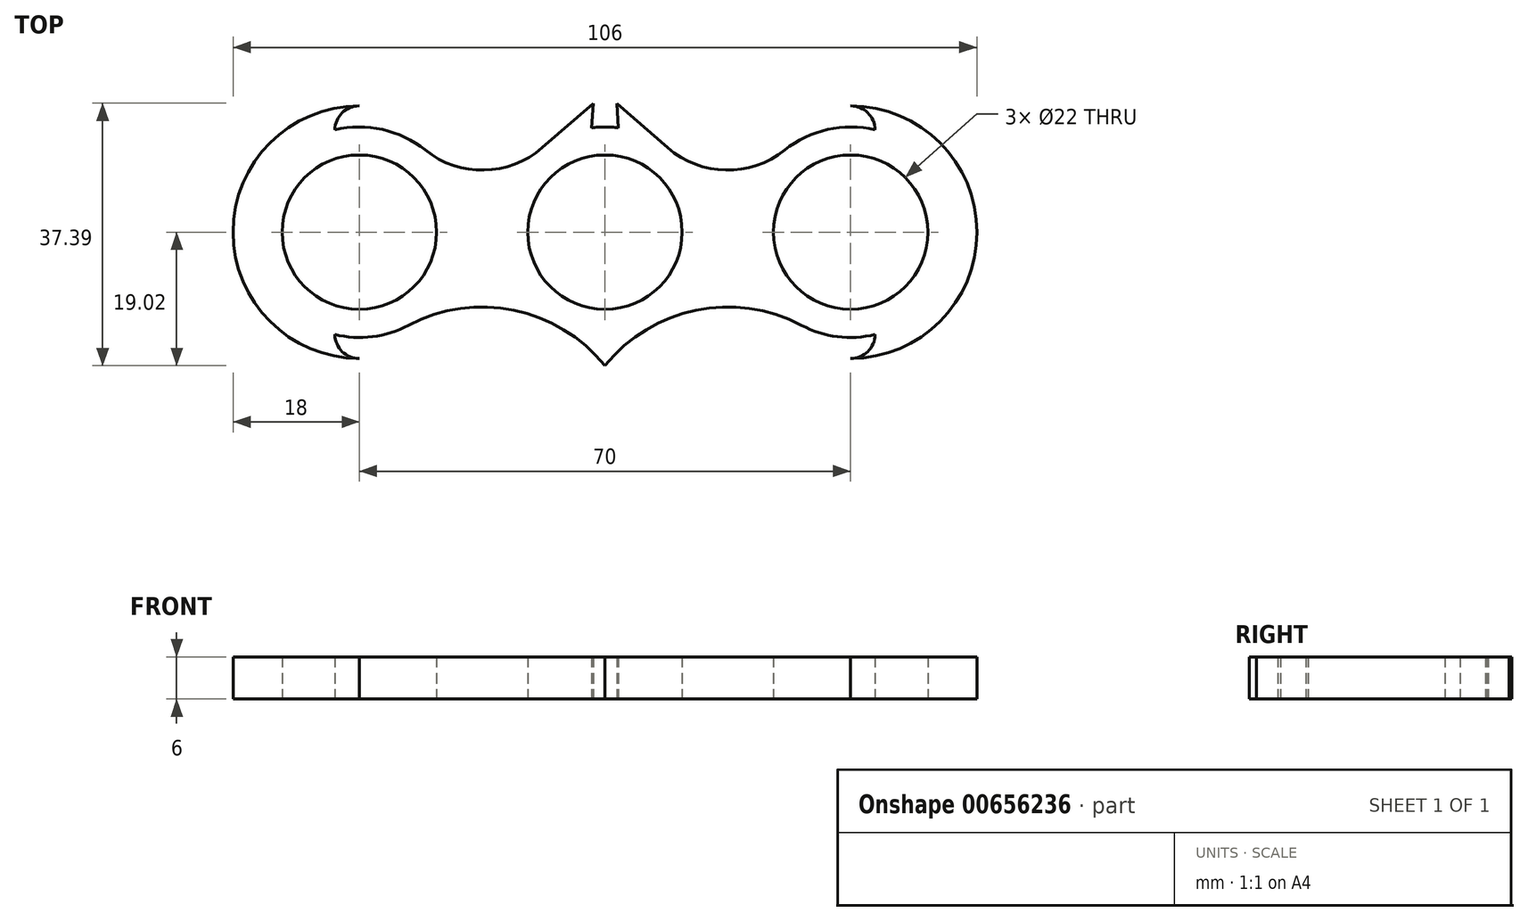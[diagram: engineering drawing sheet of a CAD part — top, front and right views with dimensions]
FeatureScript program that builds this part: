
annotation { "Feature Type Name" : "Feature", "Feature Type Description" : "" }
export const myFeature = defineFeature(function(context is Context, id is Id, definition is map)
    precondition{}
    {
        {
            var Q0;
            Q0=qCreatedBy(makeId("Top.planeOp"),FACE);
            var sketch = newSketch(context, id + "F0", { "sketchPlane" : qUnion([Q0])});
            skCircle(sketch, "E0", {"center": v(0, 0) * mm, "radius": 11 * mm});
            skArc(sketch, "E1", {"start": v(9.79, 11.37) * mm, "mid": v(9.37, 11.71) * mm, "end": v(8.95, 12.04) * mm});
            skLineSegment(sketch, "E2", {"start": v(0, 37.98) * mm, "end": v(0, -39.63) * mm, "construction": true});
            skLineSegment(sketch, "E3", {"start": v(1.92, 14.88) * mm, "end": v(1.68, 18.37) * mm});
            skLineSegment(sketch, "E4", {"start": v(1.68, 18.37) * mm, "end": v(8.95, 12.04) * mm});
            skLineSegment(sketch, "E5.MirrorCS", {"start": v(-1.92, 14.88) * mm, "end": v(-1.68, 18.37) * mm});
            skLineSegment(sketch, "E6.MirrorCS", {"start": v(-1.68, 18.37) * mm, "end": v(-8.95, 12.04) * mm});
            skLineSegment(sketch, "E7", {"start": v(-52.8, 0) * mm, "end": v(68.66, 0) * mm, "construction": true});
            skCircle(sketch, "E8", {"center": v(35, 0) * mm, "radius": 11 * mm});
            skCircle(sketch, "E9.MirrorC", {"center": v(-35, 0) * mm, "radius": 11 * mm});
            skArc(sketch, "E10", {"start": v(28, -13.27) * mm, "mid": v(33.13, -14.88) * mm, "end": v(38.5, -14.59) * mm});
            skArc(sketch, "E11.MirrorC", {"start": v(-38.5, 14.59) * mm, "mid": v(-31.72, 14.64) * mm, "end": v(-25.62, 11.7) * mm});
            skArc(sketch, "E12", {"start": v(8.95, 12.04) * mm, "mid": v(17.22, 8.85) * mm, "end": v(25.62, 11.7) * mm});
            skArc(sketch, "E13.MirrorCS", {"start": v(-8.95, 12.04) * mm, "mid": v(-17.22, 8.85) * mm, "end": v(-25.62, 11.7) * mm});
            skArc(sketch, "E14", {"start": v(0, -19.02) * mm, "mid": v(-12.97, -11.13) * mm, "end": v(-28, -13.27) * mm});
            skArc(sketch, "E15", {"start": v(-20.67, -10.9) * mm, "mid": v(-17.04, -1.14) * mm, "end": v(-19.4, 8.99) * mm, "construction": true});
            skArc(sketch, "E16", {"start": v(-38.5, 14.59) * mm, "mid": v(-37.44, 17) * mm, "end": v(-35, 18) * mm});
            skArc(sketch, "E17.MirrorC", {"start": v(-38.5, -14.59) * mm, "mid": v(-37.44, -17) * mm, "end": v(-35, -18) * mm});
            skArc(sketch, "E18.MirrorC", {"start": v(38.5, 14.59) * mm, "mid": v(37.44, 17) * mm, "end": v(35, 18) * mm});
            skArc(sketch, "E19.MirrorC", {"start": v(38.5, -14.59) * mm, "mid": v(37.44, -17) * mm, "end": v(35, -18) * mm});
            skArc(sketch, "E20.MirrorC", {"start": v(20.67, -10.9) * mm, "mid": v(17.04, -1.14) * mm, "end": v(19.4, 8.99) * mm, "construction": true});
            skArc(sketch, "E21.MirrorCS", {"start": v(0, -19.02) * mm, "mid": v(12.97, -11.13) * mm, "end": v(28, -13.27) * mm});
            skArc(sketch, "E22.trimOffspring", {"start": v(-35, 18) * mm, "mid": v(-53, 0) * mm, "end": v(-35, -18) * mm});
            skArc(sketch, "E23.trimOffspring", {"start": v(-28, -13.27) * mm, "mid": v(-33.13, -14.88) * mm, "end": v(-38.5, -14.59) * mm});
            skArc(sketch, "E24.trimOffspring", {"start": v(35, 18) * mm, "mid": v(53, 0) * mm, "end": v(35, -18) * mm});
            skArc(sketch, "E25.trimOffspring", {"start": v(38.5, 14.59) * mm, "mid": v(31.72, 14.64) * mm, "end": v(25.62, 11.7) * mm});
            skArc(sketch, "E26.trimOffspring", {"start": v(1.92, 14.88) * mm, "mid": v(0, 15) * mm, "end": v(-1.92, 14.88) * mm});
            skSolve(sketch);
        }
        {
            var Q0;
            Q0=makeQuery(id+"F0.imprint","IMPRINT",FACE,{"disambiguationData":[TD([[makeQuery(id+"F0.imprint","IMPRINT",EDGE,{"derivedFrom":sQuery(id+"F0.wireOp",EDGE,"E0")}),-1.0]])]});
            extrude(context, id + "F1", {"entities" : qUnion([Q0]), "depth" : 6 * mm, "offsetDistance" : 25 * mm});
        }
    });
